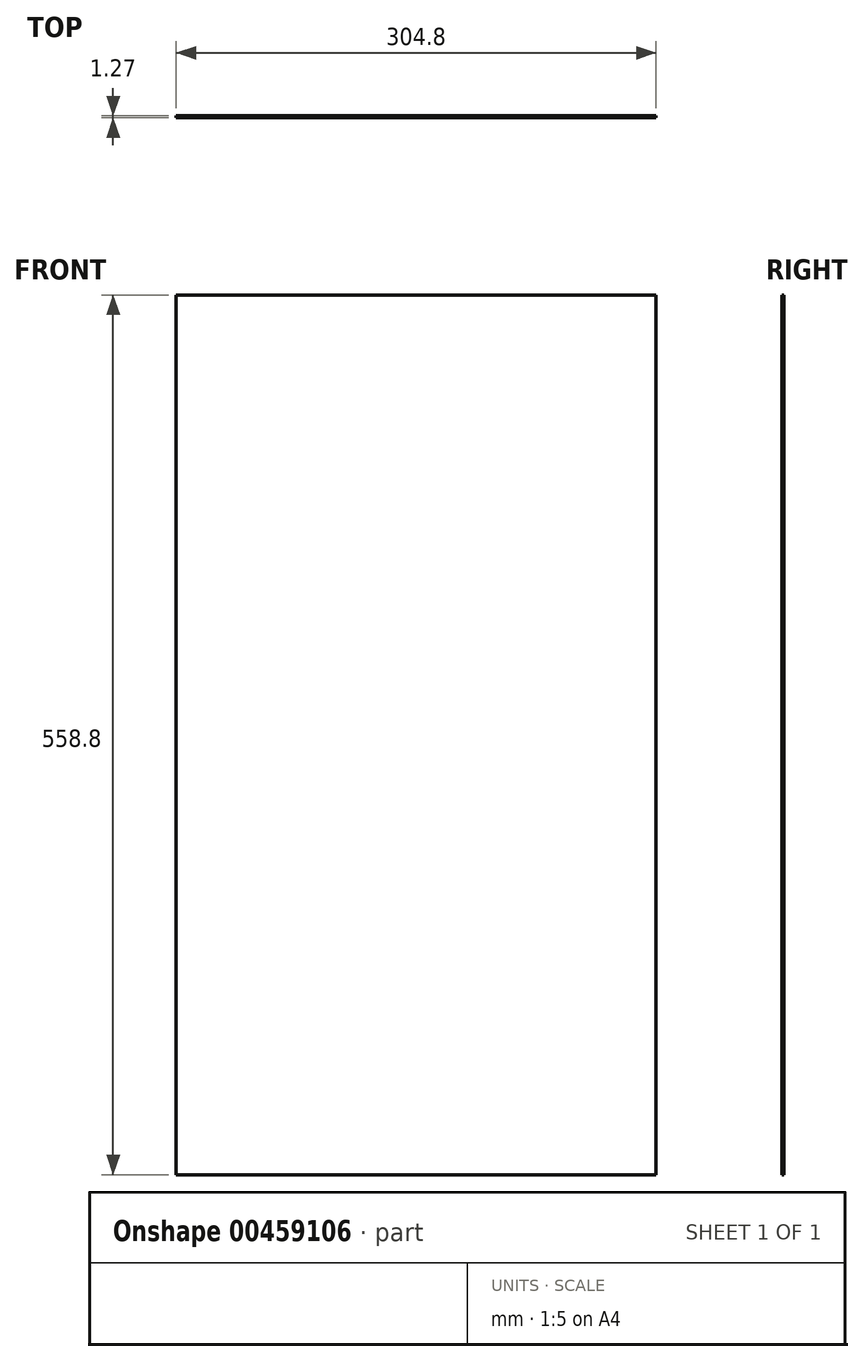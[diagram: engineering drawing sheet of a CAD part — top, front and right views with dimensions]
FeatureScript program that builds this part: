
annotation { "Feature Type Name" : "Feature", "Feature Type Description" : "" }
export const myFeature = defineFeature(function(context is Context, id is Id, definition is map)
    precondition{}
    {
        {
            var Q0;
            Q0=qCreatedBy(makeId("Front.planeOp"),FACE);
            var sketch = newSketch(context, id + "F0", { "sketchPlane" : qUnion([Q0])});
            skLineSegment(sketch, "E0.bottom", {"start": v(-318.86, 241.3) * mm, "end": v(-14.06, 241.3) * mm});
            skLineSegment(sketch, "E0.top", {"start": v(-318.86, -317.5) * mm, "end": v(-14.06, -317.5) * mm});
            skLineSegment(sketch, "E0.left", {"start": v(-318.86, 241.3) * mm, "end": v(-318.86, -317.5) * mm});
            skLineSegment(sketch, "E0.right", {"start": v(-14.06, 241.3) * mm, "end": v(-14.06, -317.5) * mm});
            skSolve(sketch);
        }
        {
            var Q0;
            Q0=makeQuery(id+"F0.imprint","IMPRINT",FACE,{"disambiguationData":[TD([[makeQuery(id+"F0.imprint","IMPRINT",EDGE,{"derivedFrom":sQuery(id+"F0.wireOp",EDGE,"E0.bottom")}),-1.0]])]});
            extrude(context, id + "F1", {"entities" : qUnion([Q0]), "depth" : 1.27 * mm});
        }
    });
